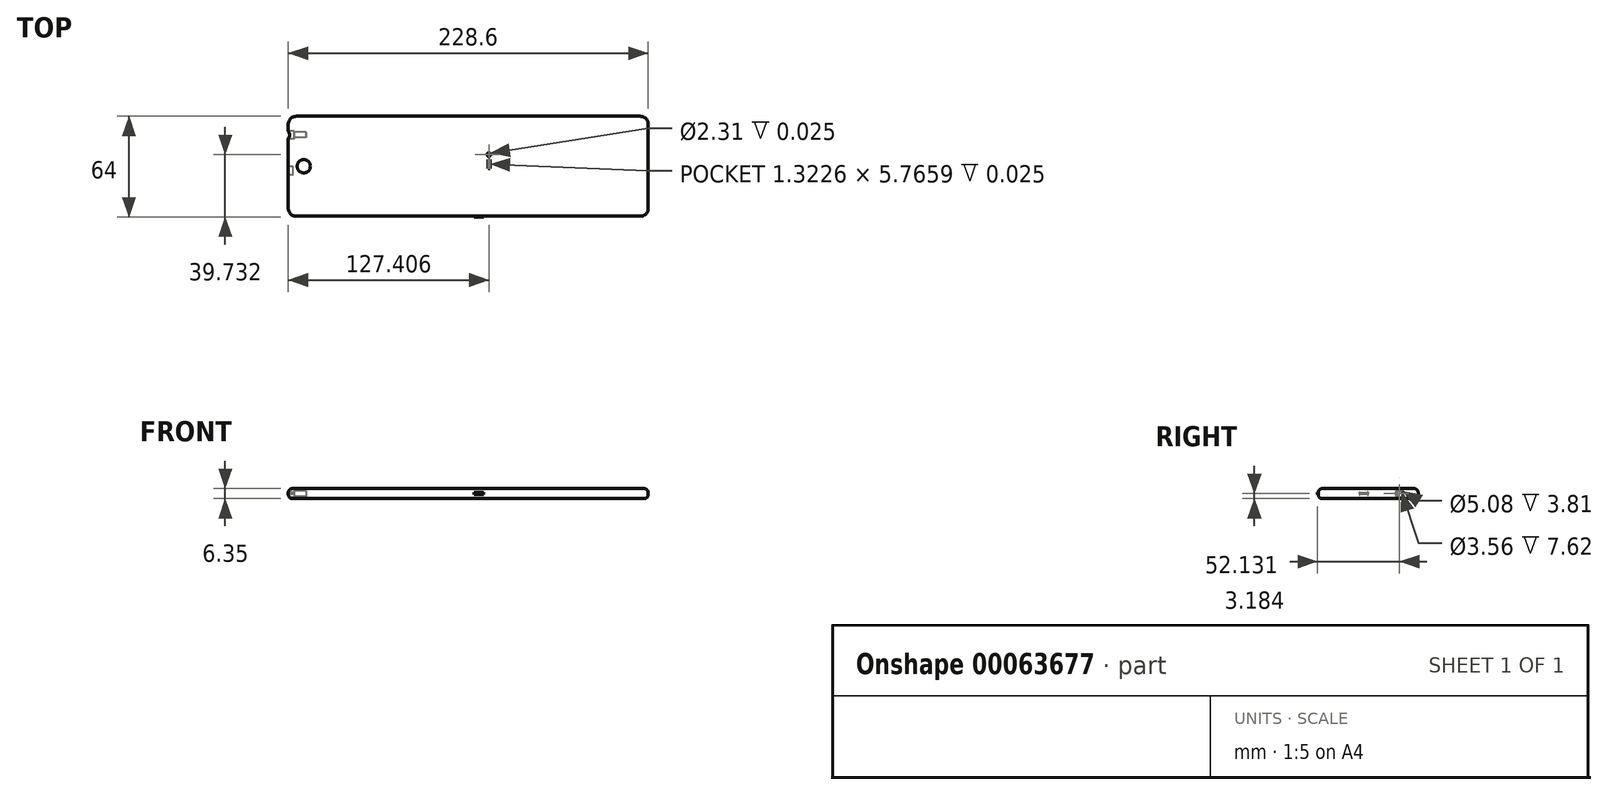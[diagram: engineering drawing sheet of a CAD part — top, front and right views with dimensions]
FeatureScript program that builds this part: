
annotation { "Feature Type Name" : "Feature", "Feature Type Description" : "" }
export const myFeature = defineFeature(function(context is Context, id is Id, definition is map)
    precondition{}
    {
        {
            var Q0;
            Q0=qCreatedBy(makeId("Top.planeOp"),FACE);
            var sketch = newSketch(context, id + "F0", { "sketchPlane" : qUnion([Q0])});
            skLineSegment(sketch, "E0.bottom", {"start": v(-66, 19.03) * mm, "end": v(162.6, 19.03) * mm});
            skLineSegment(sketch, "E0.top", {"start": v(-66, -44.47) * mm, "end": v(162.6, -44.47) * mm});
            skLineSegment(sketch, "E0.left", {"start": v(-66, 19.03) * mm, "end": v(-66, -44.47) * mm});
            skLineSegment(sketch, "E0.right", {"start": v(162.6, 19.03) * mm, "end": v(162.6, -44.47) * mm});
            skSolve(sketch);
        }
        {
            var Q0;
            Q0 = qSketchRegion(id + "F0", true);
            extrude(context, id + "F1", {"entities" : qUnion([Q0]), "depth" : 6.35 * mm});
        }
        {
            var Q0;
            Q0=makeQuery(id+"F1.opExtrude","CAP_FACE",FACE,{"disambiguationData":[OSD([sQuery(id+"F0.wireOp",EDGE,"E0.bottom"),sQuery(id+"F0.wireOp",EDGE,"E0.top"),sQuery(id+"F0.wireOp",EDGE,"E0.left"),sQuery(id+"F0.wireOp",EDGE,"E0.right")])],"isStart":false});
            fillet(context, id + "F2", {"entities" : qUnion([Q0]), "radius" : 2.54 * mm, "tangentPropagation" : true, "allowEdgeOverflow" : false});
        }
        {
            var Q0;
            Q0=makeQuery(id+"F1.opExtrude","CAP_FACE",FACE,{"disambiguationData":[OSD([sQuery(id+"F0.wireOp",EDGE,"E0.bottom"),sQuery(id+"F0.wireOp",EDGE,"E0.top"),sQuery(id+"F0.wireOp",EDGE,"E0.left"),sQuery(id+"F0.wireOp",EDGE,"E0.right")])],"isStart":true});
            fillet(context, id + "F3", {"entities" : qUnion([Q0]), "radius" : 2.54 * mm, "tangentPropagation" : true, "allowEdgeOverflow" : false});
        }
        {
            var Q0;
            Q0=makeQuery(id+"F3.opFillet","BLEND_FACE",FACE,{"disambiguationData":[OSD([sQuery(id+"F0.wireOp",EDGE,"E0.left")])]});
            var Q1;
            Q1=makeQuery(id+"F3.opFillet","BLEND_FACE",FACE,{"disambiguationData":[OSD([sQuery(id+"F0.wireOp",EDGE,"E0.bottom")])]});
            var Q2;
            Q2=makeQuery(id+"F1.opExtrude","SWEPT_FACE",FACE,{"disambiguationData":[OSD([sQuery(id+"F0.wireOp",EDGE,"E0.bottom")])]});
            var Q3;
            Q3=makeQuery(id+"F1.opExtrude","SWEPT_FACE",FACE,{"disambiguationData":[OSD([sQuery(id+"F0.wireOp",EDGE,"E0.left")])]});
            var Q4;
            Q4=makeQuery(id+"F2.opFillet","BLEND_FACE",FACE,{"disambiguationData":[OSD([sQuery(id+"F0.wireOp",EDGE,"E0.left")])]});
            var Q5;
            Q5=makeQuery(id+"F2.opFillet","BLEND_FACE",FACE,{"disambiguationData":[OSD([sQuery(id+"F0.wireOp",EDGE,"E0.bottom")])]});
            fillet(context, id + "F4", {"entities" : qUnion([Q0, Q1, Q2, Q3, Q4, Q5]), "radius" : 5.08 * mm, "tangentPropagation" : true, "allowEdgeOverflow" : false});
        }
        {
            var Q0;
            Q0=makeQuery(id+"F3.opFillet","BLEND_FACE",FACE,{"disambiguationData":[OSD([sQuery(id+"F0.wireOp",EDGE,"E0.right")])]});
            var Q1;
            Q1=makeQuery(id+"F3.opFillet","BLEND_FACE",FACE,{"disambiguationData":[OSD([sQuery(id+"F0.wireOp",EDGE,"E0.top")])]});
            var Q2;
            Q2=makeQuery(id+"F1.opExtrude","SWEPT_FACE",FACE,{"disambiguationData":[OSD([sQuery(id+"F0.wireOp",EDGE,"E0.top")])]});
            var Q3;
            Q3=makeQuery(id+"F1.opExtrude","SWEPT_FACE",FACE,{"disambiguationData":[OSD([sQuery(id+"F0.wireOp",EDGE,"E0.right")])]});
            var Q4;
            Q4=makeQuery(id+"F2.opFillet","BLEND_FACE",FACE,{"disambiguationData":[OSD([sQuery(id+"F0.wireOp",EDGE,"E0.right")])]});
            var Q5;
            Q5=makeQuery(id+"F2.opFillet","BLEND_FACE",FACE,{"disambiguationData":[OSD([sQuery(id+"F0.wireOp",EDGE,"E0.top")])]});
            fillet(context, id + "F5", {"entities" : qUnion([Q0, Q1, Q2, Q3, Q4, Q5]), "radius" : 5.08 * mm, "tangentPropagation" : true, "allowEdgeOverflow" : false});
        }
        {
            var Q0;
            Q0=makeQuery(id+"F1.opExtrude","SWEPT_FACE",FACE,{"disambiguationData":[OSD([sQuery(id+"F0.wireOp",EDGE,"E0.left")])]});
            var sketch = newSketch(context, id + "F6", { "sketchPlane" : qUnion([Q0])});
            skCircle(sketch, "E1", {"center": v(-7.16, 3.18) * mm, "radius": 2.54 * mm});
            skSolve(sketch);
        }
        {
            var Q0;
            Q0 = qSketchRegion(id + "F6", true);
            extrude(context, id + "F7", {"entities" : qUnion([Q0]), "operationType" : NewBodyOperationType.REMOVE, "oppositeDirection" : true, "depth" : 3.8 * mm});
        }
        {
            var Q0;
            Q0=makeQuery(id+"F7.boolean.opBoolean","COPY",FACE,{"derivedFrom":makeQuery(id+"F7.opExtrude","CAP_FACE",FACE,{"disambiguationData":[OSD([sQuery(id+"F6.wireOp",EDGE,"E1")])],"isStart":false})});
            var sketch = newSketch(context, id + "F8", { "sketchPlane" : qUnion([Q0])});
            skCircle(sketch, "E2", {"center": v(-7.16, 3.18) * mm, "radius": 1.78 * mm});
            skSolve(sketch);
        }
        {
            var Q0;
            Q0 = qSketchRegion(id + "F8", true);
            extrude(context, id + "F9", {"entities" : qUnion([Q0]), "operationType" : NewBodyOperationType.REMOVE, "oppositeDirection" : true, "depth" : 7.62 * mm});
        }
        {
            var Q0;
            {var subQ0=sQuery(id+"F0.wireOp",EDGE,"E0.left");var subQ1=sQuery(id+"F0.wireOp",EDGE,"E0.top");Q0=makeQuery(id+"F7.boolean.opBoolean","SPLIT",FACE,{"disambiguationData":[TD([makeQuery(id+"F4.opFillet","BLEND_FACE",FACE,{"disambiguationData":[OSD([subQ1,subQ0]),TDD([makeQuery(id+"F2.opFillet","BLEND_EDGE",EDGE,{"blendedFrom":[makeQuery(id+"F1.opExtrude","CAP_EDGE",EDGE,{"disambiguationData":[OSD([subQ1])],"isStart":false}),makeQuery(id+"F1.opExtrude","CAP_EDGE",EDGE,{"disambiguationData":[OSD([subQ0])],"isStart":false})],"blendedInto":[]})])]})])],"derivedFrom":makeQuery(id+"F1.opExtrude","SWEPT_FACE",FACE,{"disambiguationData":[OSD([subQ0])]})});}
            var sketch = newSketch(context, id + "F10", { "sketchPlane" : qUnion([Q0])});
            skLineSegment(sketch, "E3.bottom", {"start": v(12.83, 3.81) * mm, "end": v(18.28, 3.81) * mm});
            skLineSegment(sketch, "E3.top", {"start": v(12.83, 2.54) * mm, "end": v(18.28, 2.54) * mm});
            skLineSegment(sketch, "E3.left", {"start": v(12.83, 3.81) * mm, "end": v(12.83, 2.54) * mm});
            skLineSegment(sketch, "E3.right", {"start": v(18.28, 3.81) * mm, "end": v(18.28, 2.54) * mm});
            skSolve(sketch);
        }
        {
            var Q0;
            Q0 = qSketchRegion(id + "F10", true);
            extrude(context, id + "F11", {"entities" : qUnion([Q0]), "operationType" : NewBodyOperationType.REMOVE, "oppositeDirection" : true, "depth" : 3.17 * mm});
        }
        {
            var Q0;
            Q0=makeQuery(id+"F11.boolean.opBoolean","COPY",FACE,{"derivedFrom":makeQuery(id+"F11.opExtrude","SWEPT_FACE",FACE,{"disambiguationData":[OSD([sQuery(id+"F10.wireOp",EDGE,"E3.left")])]})});
            var Q1;
            Q1=makeQuery(id+"F11.boolean.opBoolean","COPY",FACE,{"derivedFrom":makeQuery(id+"F11.opExtrude","SWEPT_FACE",FACE,{"disambiguationData":[OSD([sQuery(id+"F10.wireOp",EDGE,"E3.top")])]})});
            var Q2;
            Q2=makeQuery(id+"F11.boolean.opBoolean","COPY",FACE,{"derivedFrom":makeQuery(id+"F11.opExtrude","SWEPT_FACE",FACE,{"disambiguationData":[OSD([sQuery(id+"F10.wireOp",EDGE,"E3.right")])]})});
            var Q3;
            Q3=makeQuery(id+"F11.boolean.opBoolean","COPY",FACE,{"derivedFrom":makeQuery(id+"F11.opExtrude","SWEPT_FACE",FACE,{"disambiguationData":[OSD([sQuery(id+"F10.wireOp",EDGE,"E3.bottom")])]})});
            fillet(context, id + "F12", {"entities" : qUnion([Q0, Q1, Q2, Q3]), "radius" : 0.25 * mm, "tangentPropagation" : true, "allowEdgeOverflow" : false});
        }
        {
            var Q0;
            Q0=makeQuery(id+"F1.opExtrude","SWEPT_FACE",FACE,{"disambiguationData":[OSD([sQuery(id+"F0.wireOp",EDGE,"E0.top")])]});
            var sketch = newSketch(context, id + "F13", { "sketchPlane" : qUnion([Q0])});
            skLineSegment(sketch, "E4.bottom", {"start": v(52.02, 3.81) * mm, "end": v(58.12, 3.81) * mm});
            skLineSegment(sketch, "E4.top", {"start": v(52.02, 2.54) * mm, "end": v(58.12, 2.54) * mm});
            skLineSegment(sketch, "E4.left", {"start": v(52.02, 3.81) * mm, "end": v(52.02, 2.54) * mm});
            skLineSegment(sketch, "E4.right", {"start": v(58.12, 3.81) * mm, "end": v(58.12, 2.54) * mm});
            skSolve(sketch);
        }
        {
            var Q0;
            Q0 = qSketchRegion(id + "F13", true);
            extrude(context, id + "F14", {"entities" : qUnion([Q0]), "operationType" : NewBodyOperationType.ADD, "depth" : 0.5 * mm});
        }
        {
            var Q0;
            Q0=makeQuery(id+"F1.opExtrude","CAP_FACE",FACE,{"disambiguationData":[OSD([sQuery(id+"F0.wireOp",EDGE,"E0.bottom"),sQuery(id+"F0.wireOp",EDGE,"E0.top"),sQuery(id+"F0.wireOp",EDGE,"E0.left"),sQuery(id+"F0.wireOp",EDGE,"E0.right")])],"isStart":false});
            var sketch = newSketch(context, id + "F15", { "sketchPlane" : qUnion([Q0])});
            skCircle(sketch, "E5", {"center": v(-56.2, -12.72) * mm, "radius": 4.2 * mm});
            skPoint(sketch, "E5.centerSnap0", {"position": v(-63.45, -12.72) * mm});
            skSolve(sketch);
        }
        {
            var Q0;
            Q0 = qSketchRegion(id + "F15", true);
            extrude(context, id + "F16", {"entities" : qUnion([Q0]), "operationType" : NewBodyOperationType.REMOVE, "oppositeDirection" : true, "depth" : 0.25 * mm});
        }
        {
            var Q0;
            Q0=makeQuery(id+"F16.boolean.opBoolean","COPY",FACE,{"derivedFrom":makeQuery(id+"F16.opExtrude","SWEPT_FACE",FACE,{"disambiguationData":[OSD([sQuery(id+"F15.wireOp",EDGE,"E5")])]})});
            var Q1;
            Q1=makeQuery(id+"F16.boolean.opBoolean","COPY",FACE,{"derivedFrom":makeQuery(id+"F16.opExtrude","CAP_FACE",FACE,{"disambiguationData":[OSD([sQuery(id+"F15.wireOp",EDGE,"E5")])],"isStart":false})});
            fillet(context, id + "F17", {"entities" : qUnion([Q0, Q1]), "radius" : 0.13 * mm, "tangentPropagation" : true, "allowEdgeOverflow" : false});
        }
        {
            var Q0;
            Q0=makeQuery(id+"F1.opExtrude","CAP_FACE",FACE,{"disambiguationData":[OSD([sQuery(id+"F0.wireOp",EDGE,"E0.bottom"),sQuery(id+"F0.wireOp",EDGE,"E0.top"),sQuery(id+"F0.wireOp",EDGE,"E0.left"),sQuery(id+"F0.wireOp",EDGE,"E0.right")])],"isStart":false});
            var sketch = newSketch(context, id + "F18", { "sketchPlane" : qUnion([Q0])});
            skLineSegment(sketch, "E6.bottom", {"start": v(62.08, -14.16) * mm, "end": v(60.76, -14.16) * mm});
            skLineSegment(sketch, "E6.top", {"start": v(62.08, -8.4) * mm, "end": v(60.76, -8.4) * mm});
            skLineSegment(sketch, "E6.left", {"start": v(62.08, -14.16) * mm, "end": v(62.08, -8.4) * mm});
            skLineSegment(sketch, "E6.right", {"start": v(60.76, -14.16) * mm, "end": v(60.76, -8.4) * mm});
            skCircle(sketch, "E7", {"center": v(61.42, -5.24) * mm, "radius": 1.15 * mm});
            skPoint(sketch, "E7.centerSnap0", {"position": v(61.42, -8.4) * mm});
            skSolve(sketch);
        }
        {
            var Q0;
            Q0 = qSketchRegion(id + "F18", true);
            extrude(context, id + "F19", {"entities" : qUnion([Q0]), "operationType" : NewBodyOperationType.REMOVE, "oppositeDirection" : true, "depth" : 0.03 * mm});
        }
    });
